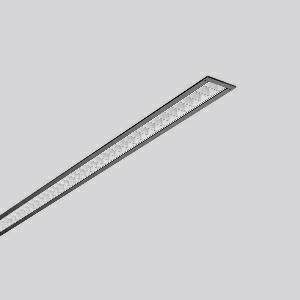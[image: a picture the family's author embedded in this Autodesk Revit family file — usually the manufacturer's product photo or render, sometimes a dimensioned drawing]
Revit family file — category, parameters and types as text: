
# Revit family: less_is_more_27_312177_003_ca46
name_source: partatom
category: Lighting Fixtures
units: mm (PartAtom-declared; Revit-internal decimal feet)

## family parameters
Cut with Voids When Loaded = No
Host = Face
Light Source = No
Part Type = Normal
Room Calculation Point = No
Round Connector Dimension = Use Diameter
Shared = No

## types (1)
- LESS IS MORE 27 (1 x LED Modul 830, 2350 lm, 3000)
    Apparent Load = 29 VA
    CIE Flux Codes = 90 99 100 100 100
    Color Rendering = 80
    Color Temperature = 3000
    Default Elevation = 1800 mm
    Description = Series: LESS IS MORE 27
Recessed ceiling and wall luminaire with slim design. Housing: extruded aluminium profile, powder-coated. End cap aluminium powder-coated. High polish aluminium micro grid. Perfect for office areas (RUG < 19) and environments with computer screens in accordance with EN 12464-1. Suitable for Recessed ceiling mounting, wall (recessed). External driver with connecting cable. 
Colour: deep black, matt (RAL 9005)
Length: 1014 mm
Width: 38 mm
Height: 2 mm
Cut-out length: 1006 mm
Cut-out width: 30 mm
Recess height: 45-60 mm
Luminaire: recess height: 37 mm
Lamp: LED
Socket: without socket
Colour temperature: 3000K
Colour rendering index (CRI): 82
System power: 29 W
Rated luminous flux: 2350 lm
Luminous efficiency: 81 lm/W
Control gear: Regulated power supply
Protection class: II
Type of protection: IP 20
    Height = 0 mm  [stored 0 ft]
    Lamp = 1 x LED Modul 830
    Lamp Light Flux = 2350 lm
    Lamp count = 1
    Length = 1014 mm
    Lifetime = 50000 h
    Luminous efficacy = 81 lm/W
    Manufacturer = RZB
    ModVariant = No
    Model = 312177.003
    Mounting Place = Ceiling, Wall
    Mounting Type = Recessed
    Number of Poles = 1
    OnlyDefault = Yes
    Power Factor = 1
    Product Name = LESS IS MORE 27
    Product group = Recessed LED linear luminaires
    ProductGroupID = 407
    Protection Class = Protection class II
    Protection Degree = IP 20
    RLX_Detail_Level = 1
    RLX_Emergency_Light_Flux = 0 lm
    RLX_Emergency_Type = 0
    RLX_Emergency_Type_DB = No
    RlxData = <blob elided: 29885 chars, md5=0a2e9fca>
    Socket = socket
    Standby Power = 0 W
    System Light Flux = 2350 lm
    System Power = 29 W
    Type Comments = Product without accessories
    Type Image = 312177.003.jpg
    URL = http://relux.com
    VarID = ---
    Voltage = 230 V
    Voltage Range = 220-240 V
    Weight = 0.00 kg
    Width = 38 mm

note: [stored X ft] marks values corroborated as IEEE doubles in the binary element streams (Revit-internal decimal feet)

## geometry (parser evidence)
native form markers: Blend x4, Sweep x10
no freeform markers — native parametric forms only
